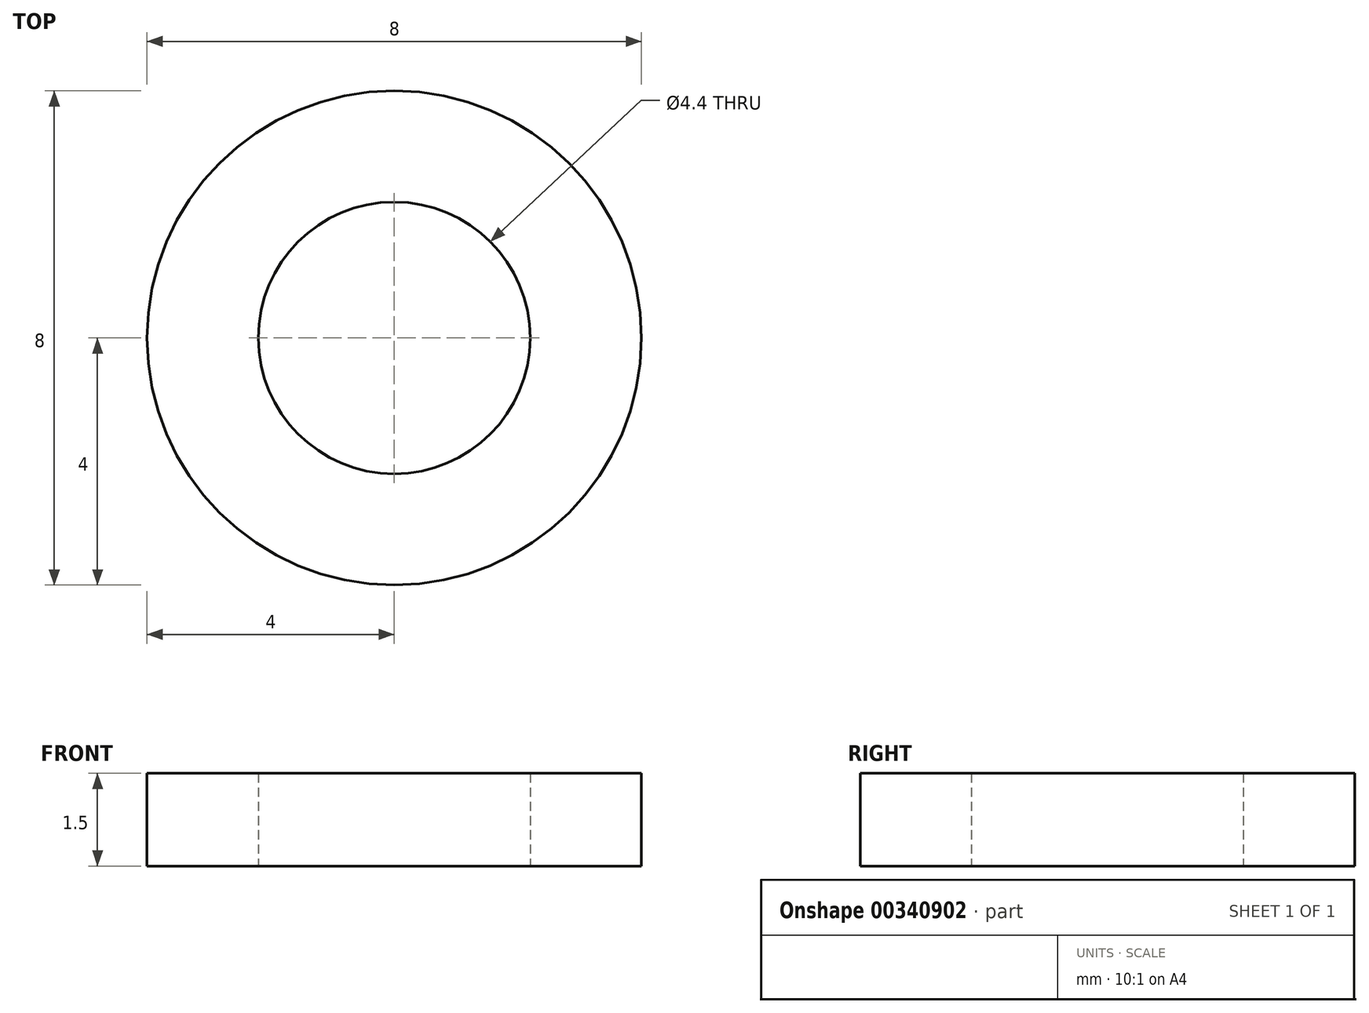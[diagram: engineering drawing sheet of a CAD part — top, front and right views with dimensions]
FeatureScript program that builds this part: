
annotation { "Feature Type Name" : "Feature", "Feature Type Description" : "" }
export const myFeature = defineFeature(function(context is Context, id is Id, definition is map)
    precondition{}
    {
        {
            var Q0;
            Q0=qCreatedBy(makeId("Top.planeOp"),FACE);
            var sketch = newSketch(context, id + "F0", { "sketchPlane" : qUnion([Q0])});
            skCircle(sketch, "E0", {"center": v(0, 0) * mm, "radius": 2.2 * mm});
            skCircle(sketch, "E1", {"center": v(0, 0) * mm, "radius": 4 * mm});
            skSolve(sketch);
        }
        {
            var Q0;
            Q0=makeQuery(id+"F0.imprint","IMPRINT",FACE,{"disambiguationData":[TD([[makeQuery(id+"F0.imprint","IMPRINT",EDGE,{"derivedFrom":sQuery(id+"F0.wireOp",EDGE,"E0")}),-1.0]])]});
            extrude(context, id + "F1", {"entities" : qUnion([Q0]), "depth" : 1.5 * mm, "offsetDistance" : 25 * mm});
        }
    });
